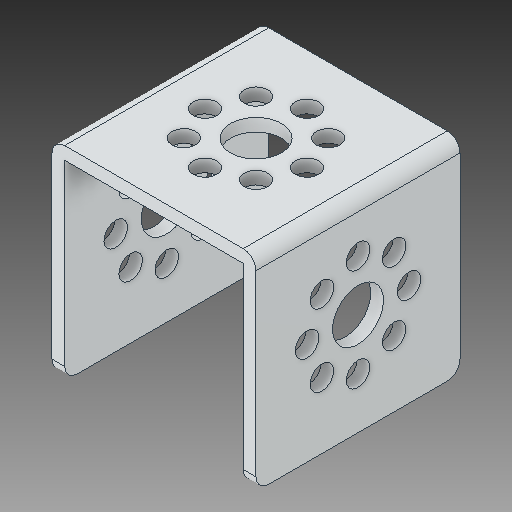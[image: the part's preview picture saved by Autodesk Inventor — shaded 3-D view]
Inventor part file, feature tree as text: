
AUTODESK INVENTOR PART (.ipt)
format: ipt  version: 2018 (Build 220112000, 112)  size: 212,480 bytes
history: native  units: in
note: dims shown in document units (in); Inventor stores cm internally (conversion verified against a paired STEP export)
features: fillet x1
ambient origin geometry x8: Origin, YZ Plane, XZ Plane, XY Plane, X Axis, Y Axis, Z Axis, Center Point
bodies: Solid1 (feature_tree)
feature tree (1):
  fillet  "Fillet1"  [1 undecoded]
note: 1 required parameter value undecoded (feature->parameter linkage not recoverable at this tier; creation-order binding heuristic only, values carry confidence <= 0.55)
